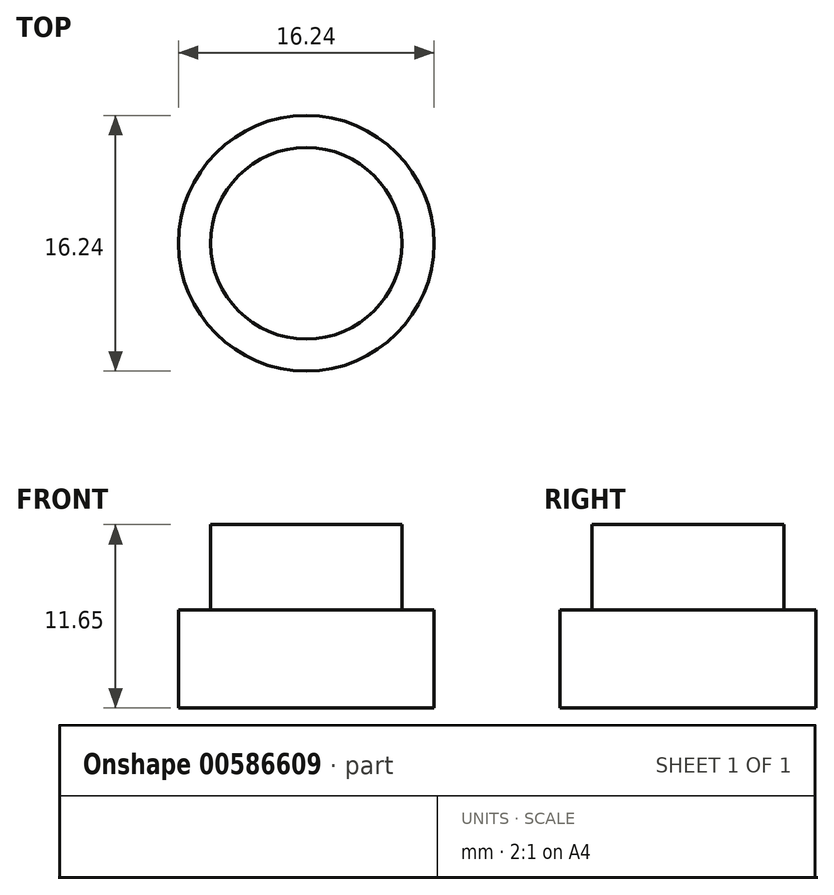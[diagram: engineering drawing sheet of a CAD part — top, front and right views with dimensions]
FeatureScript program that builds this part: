
annotation { "Feature Type Name" : "Feature", "Feature Type Description" : "" }
export const myFeature = defineFeature(function(context is Context, id is Id, definition is map)
    precondition{}
    {
        {
            var Q0;
            Q0=qCreatedBy(makeId("Top.planeOp"),FACE);
            var sketch = newSketch(context, id + "F0", { "sketchPlane" : qUnion([Q0])});
            skCircle(sketch, "E0", {"center": v(0, 0) * mm, "radius": 8.12 * mm});
            skSolve(sketch);
        }
        {
            var Q0;
            Q0=qCreatedBy(makeId("Right.planeOp"),FACE);
            var sketch = newSketch(context, id + "F1", { "sketchPlane" : qUnion([Q0])});
            skLineSegment(sketch, "E1", {"start": v(0, 0) * mm, "end": v(0, -6.24) * mm});
            skSolve(sketch);
        }
        {
            var Q0;
            Q0 = qSketchRegion(id + "F1", true);
            var Q1;
            Q1 = qSketchRegion(id + "F0", true);
            var Q2;
            Q2=sQuery(id+"F1.wireOp",EDGE,"E1");
            sweep(context, id + "F2", {"profiles" : qUnion([Q0, Q1]), "path" : qUnion([Q2])});
        }
        {
            var Q0;
            Q0=qCreatedBy(makeId("Top.planeOp"),FACE);
            var sketch = newSketch(context, id + "F3", { "sketchPlane" : qUnion([Q0])});
            skCircle(sketch, "E2", {"center": v(0, 0) * mm, "radius": 6.08 * mm});
            skSolve(sketch);
        }
        {
            var Q0;
            Q0=qCreatedBy(makeId("Right.planeOp"),FACE);
            var sketch = newSketch(context, id + "F4", { "sketchPlane" : qUnion([Q0])});
            skLineSegment(sketch, "E3", {"start": v(0, 0) * mm, "end": v(0, 5.4) * mm});
            skSolve(sketch);
        }
        {
            var Q0;
            Q0 = qSketchRegion(id + "F3", true);
            var Q1;
            Q1=sQuery(id+"F4.wireOp",EDGE,"E3");
            sweep(context, id + "F5", {"operationType" : NewBodyOperationType.ADD, "profiles" : qUnion([Q0]), "path" : qUnion([Q1])});
        }
    });
